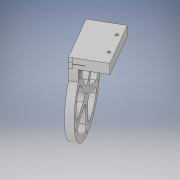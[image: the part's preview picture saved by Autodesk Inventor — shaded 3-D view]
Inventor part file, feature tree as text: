
AUTODESK INVENTOR PART (.ipt)
format: ipt  version: 2017 (Build 210142000, 142)  size: 361,984 bytes
history: native  units: in
note: dims shown in document units (in); Inventor stores cm internally (conversion verified against a paired STEP export)
features: extrude x10, sketch x10, projected_geometry x7, plane x1, imported_body x1
ambient origin geometry x8: Origin, YZ Plane, XZ Plane, XY Plane, X Axis, Y Axis, Z Axis, Center Point
bodies: Solid1 (feature_tree)
feature tree (29):
  extrude  "Extrusion1"  Depth=0.3937in TaperAngle=0.0deg
  extrude  "Extrusion2"  Depth=0.1969in
  extrude  "Extrusion3"  Depth=0.125in
  extrude  "Extrusion4"  Depth=0.3937in TaperAngle=0.0deg
  extrude  "Extrusion5"  Depth=0.7087in
  plane  "Work Plane1"
  extrude  "Extrusion6"  Depth=0.9154in
  extrude  "Extrusion7"  Depth=0.1969in
  extrude  "Extrusion8"  Depth=1.3091in
  extrude  "Extrusion9"  Depth=0.0787in TaperAngle=0.0deg
  extrude  "Extrusion10"  Depth=0.125in
  sketch  "Sketch1"  dims[d0=1.25in d1=0.0in d2=0.3937in d3=0.0in]
  projected_geometry  "Projected Loop1"
  projected_geometry  "Projected Loop2"
  projected_geometry  "Projected Loop3"
  sketch  "Sketch2"  dims[d4=0.1969in d5=0.0in d6=0.375in]
  sketch  "Sketch3"  dims[d7=0.5in d8=0.125in]
  projected_geometry  "Projected Loop4"
  sketch  "Sketch4"  dims[d9=0.3937in d10=0.0in d11=0.1875in d12=0.0in]
  sketch  "Sketch5"  dims[d13=3.2677in d19=0.7087in]
  projected_geometry  "Projected Loop5"
  sketch  "Sketch8"  dims[d20=0.6102in d21=0.9154in]
  sketch  "Sketch9"  dims[d22=0.6102in d23=0.1969in]
  sketch  "Sketch11"  dims[d24=0.0787in d25=1.3091in]
  sketch  "Sketch13"  dims[d26=0.6693in d27=0.0in d28=0.0787in d29=0.0in]
  projected_geometry  "Projected Loop8"
  sketch  "Sketch14"  dims[d30=0.0787in d31=0.0in d32=0.125in d33=0.0in d34=0.0787in d35=0.0in d36=0.0787in d37=90.0deg d38=0.5118in d39=0.0787in d40=0.0in]
  projected_geometry  "Projected Loop9"
  imported_body  "Base1"
